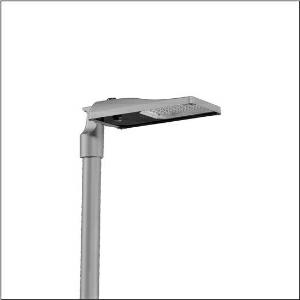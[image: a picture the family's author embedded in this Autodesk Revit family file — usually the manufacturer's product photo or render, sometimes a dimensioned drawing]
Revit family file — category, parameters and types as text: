
# Revit family: streetlight_sl_31_mini___st0_8a_5xh6c31t08ga_5d86
name_source: partatom
category: Lighting Fixtures
units: mm (PartAtom-declared; Revit-internal decimal feet)

## family parameters
Cut with Voids When Loaded = No
Host = Face
Light Source = No
Part Type = Normal
Room Calculation Point = No
Round Connector Dimension = Use Diameter
Shared = No

## types (1)
- --- (1 x LED, 5880 lm, 39.3 W, 3000K)
    Apparent Load = 39 VA
    CIE Flux Codes = 38 75 97 100 100
    Color Rendering = 70
    Color Temperature = 3000K
    Default Elevation = 1800 mm
    Description = Streetlight SL 31 mini D4i, Desk-Remote mast luminaire for post-top, side-entry; light control with lens of PMMA; light distribution: ST0.8a, direct asymmetric distribution, for standard-compliant lighting for roads and squares; LED: luminous flux: 5.880lm, light colour: 730, colour temperature: 3000K; luminous efficacy: 149,6lm/W; control: pre-setting: logarithmic dimming characteristic, flexible luminous flux parameterisation, time-dependent luminous flux control, constant luminous flux control, power reduction, intelligent temperature release in ECG and LED module, overheat protection; luminaire housing, of diecast aluminium, SITECO metallic grey (DB 702S), corrosivity category C5 high according to DIN EN ISO 12944; cover of toughened safety glass, transparent, opened without tools; mast flange of diecast aluminium, SITECO metallic grey (DB 702S), spigot size: 76/60mm, mast flange included unmounted; with cable H07RN-F 2x 1.5mm², cable length: 6,5m, connection cable pre-assembled; mains connection: 220..240V, AC, 50/60Hz; power consumption (at start of service life): 39,3W / (at end of service life): 40,7W / (with reduced operation 50%): 18,1W; protection rating (complete): IP66; insulation class (complete): insulation class II (safety insulation); impact resistance: IK09; certification: CE, ENEC, ENEC+, VDE, UKCA, ZD4i; permissible operating ambient temperature for outdoor applications: -40..+50°C; packaging unit: 1 piece

Light Distribution: ST0.8a
    Height = 76 mm
    Lamp = 1 x LED
    Lamp Light Flux = 5880 lm
    Lamp Power = 39.3 W
    Lamp count = 1
    Length = 547 mm
    Luminous efficacy = 150 lm/W
    Manufacturer = Siteco
    ModVariant = No
    Model = 5XH6C31T08GA
    Number of Poles = 1
    OnlyDefault = Yes
    Power Factor = 1
    Product Name = Streetlight SL 31 mini | ST0.8a
    Product group = mast luminaire | pylon top
    ProductGroupID = 6100
    Protection Class = Protection class II
    Protection Degree = IP 66
    RLX_Detail_Level = 1
    RLX_Emergency_Light_Flux = 0 lm
    RLX_Emergency_Type = 0
    RLX_Emergency_Type_DB = No
    RlxData = <blob elided: 39961 chars, md5=d89d972d>
    Socket = socket
    Standby Power = 0 W
    System Light Flux = 5880 lm
    System Power = 39 W
    Type Comments = factory setting: luminous flux: 100 % | dim-lin: 254 | 798 mA
    Type Image = l_1300332.jpg
    URL = http://relux.com
    VarID = @adj_056569
    Voltage = 0 V
    Weight = 0.00 kg
    Width = 265 mm

## geometry (parser evidence)
native form markers: Blend x4, Sweep x10
no freeform markers — native parametric forms only
